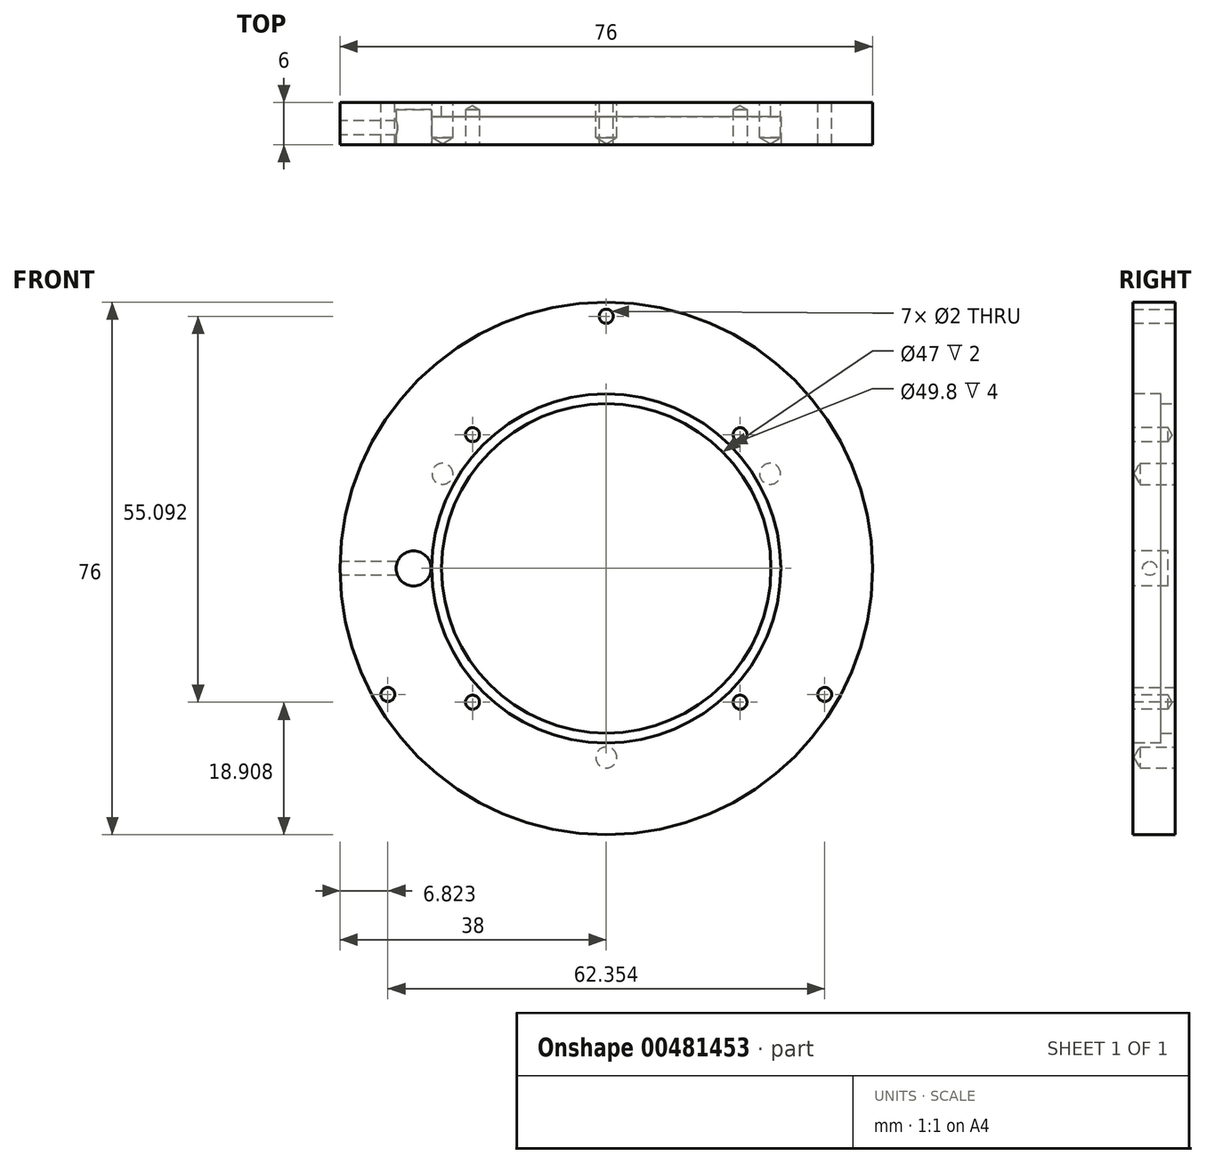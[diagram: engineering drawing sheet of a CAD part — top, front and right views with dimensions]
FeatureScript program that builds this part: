
annotation { "Feature Type Name" : "Feature", "Feature Type Description" : "" }
export const myFeature = defineFeature(function(context is Context, id is Id, definition is map)
    precondition{}
    {
        {
            var Q0;
            Q0=qCreatedBy(makeId("Front.planeOp"),FACE);
            var sketch = newSketch(context, id + "F0", { "sketchPlane" : qUnion([Q0])});
            skCircle(sketch, "E0", {"center": v(0, 0) * mm, "radius": 38 * mm});
            skCircle(sketch, "E1", {"center": v(0, 0) * mm, "radius": 23.5 * mm});
            skSolve(sketch);
        }
        {
            var Q0;
            Q0 = qSketchRegion(id + "F0", true);
            extrude(context, id + "F1", {"entities" : qUnion([Q0]), "depth" : 6 * mm});
        }
        {
            var Q0;
            Q0=makeQuery(id+"F1.opExtrude","CAP_FACE",FACE,{"disambiguationData":[OSD([sQuery(id+"F0.wireOp",EDGE,"E0"),sQuery(id+"F0.wireOp",EDGE,"E1")])],"isStart":false});
            var sketch = newSketch(context, id + "F2", { "sketchPlane" : qUnion([Q0])});
            skCircle(sketch, "E2", {"center": v(0, 0) * mm, "radius": 24.9 * mm});
            skSolve(sketch);
        }
        {
            var Q0;
            Q0 = qSketchRegion(id + "F2", true);
            extrude(context, id + "F3", {"entities" : qUnion([Q0]), "operationType" : NewBodyOperationType.REMOVE, "oppositeDirection" : true, "depth" : 4 * mm});
        }
        {
            var Q0;
            Q0=makeQuery(id+"F1.opExtrude","CAP_FACE",FACE,{"disambiguationData":[OSD([sQuery(id+"F0.wireOp",EDGE,"E0"),sQuery(id+"F0.wireOp",EDGE,"E1")])],"isStart":true});
            var sketch = newSketch(context, id + "F4", { "sketchPlane" : qUnion([Q0])});
            skPoint(sketch, "E3", {"position": v(23.38, 13.5) * mm});
            skLineSegment(sketch, "E4", {"start": v(0, 0) * mm, "end": v(35.09, 20.26) * mm, "construction": true});
            skLineSegment(sketch, "E5", {"start": v(0, 0) * mm, "end": v(-35.23, 20.34) * mm, "construction": true});
            skLineSegment(sketch, "E6", {"start": v(0, 0) * mm, "end": v(0, -41.92) * mm, "construction": true});
            skLineSegment(sketch, "E7", {"start": v(0, 0) * mm, "end": v(-35.01, -20.21) * mm, "construction": true});
            skLineSegment(sketch, "E8", {"start": v(0, 0) * mm, "end": v(34, -19.63) * mm, "construction": true});
            skLineSegment(sketch, "E9", {"start": v(0, 0) * mm, "end": v(0, 41.54) * mm, "construction": true});
            skCircle(sketch, "E10", {"center": v(0, 0) * mm, "radius": 27 * mm, "construction": true});
            skPoint(sketch, "E11", {"position": v(-23.38, 13.5) * mm});
            skPoint(sketch, "E12", {"position": v(-31.18, -18) * mm});
            skPoint(sketch, "E13", {"position": v(0, -27) * mm});
            skPoint(sketch, "E14", {"position": v(31.18, -18) * mm});
            skCircle(sketch, "E15", {"center": v(0, 0) * mm, "radius": 36 * mm, "construction": true});
            skPoint(sketch, "E16", {"position": v(0, 36) * mm});
            skSolve(sketch);
        }
        {
            var Q0;
            Q0=sQuery(id+"F4.wireOp",VERTEX,"E3");
            var Q1;
            Q1=sQuery(id+"F4.wireOp",VERTEX,"E11");
            var Q2;
            Q2=sQuery(id+"F4.wireOp",VERTEX,"E13");
            var Q3;
            Q3=makeQuery(id+"F1.opExtrude","SWEPT_BODY",BODY,{"disambiguationData":[OSD([sQuery(id+"F0.wireOp",EDGE,"E0"),sQuery(id+"F0.wireOp",EDGE,"E1")])]});
            hole(context, id + "F5", {"style" : HoleStyle.SIMPLE, "endStyle" : HoleEndStyle.BLIND, "holeDiameter" : 3 * mm, "holeDepth" : 5 * mm, "isTappedThrough" : true, "tappedDepth" : 12 * mm, "tapClearance" : 3, "locations" : qUnion([Q0, Q1, Q2]), "scope" : qUnion([Q3])});
        }
        {
            var Q0;
            Q0=sQuery(id+"F4.wireOp",VERTEX,"E16");
            var Q1;
            Q1=sQuery(id+"F4.wireOp",VERTEX,"E12");
            var Q2;
            Q2=sQuery(id+"F4.wireOp",VERTEX,"E14");
            var Q3;
            Q3=makeQuery(id+"F1.opExtrude","SWEPT_BODY",BODY,{"disambiguationData":[OSD([sQuery(id+"F0.wireOp",EDGE,"E0"),sQuery(id+"F0.wireOp",EDGE,"E1")])]});
            hole(context, id + "F6", {"style" : HoleStyle.SIMPLE, "endStyle" : HoleEndStyle.THROUGH, "holeDiameter" : 2 * mm, "isTappedThrough" : true, "tappedDepth" : 12 * mm, "tapClearance" : 3, "locations" : qUnion([Q0, Q1, Q2]), "scope" : qUnion([Q3])});
        }
        {
            var Q0;
            Q0=makeQuery(id+"F1.opExtrude","CAP_FACE",FACE,{"disambiguationData":[OSD([sQuery(id+"F0.wireOp",EDGE,"E0"),sQuery(id+"F0.wireOp",EDGE,"E1")])],"isStart":false});
            var sketch = newSketch(context, id + "F7", { "sketchPlane" : qUnion([Q0])});
            skCircle(sketch, "E17", {"center": v(0, 0) * mm, "radius": 27 * mm, "construction": true});
            skLineSegment(sketch, "E18", {"start": v(0, 0) * mm, "end": v(37.63, 37.63) * mm, "construction": true});
            skLineSegment(sketch, "E19", {"start": v(-32.63, -32.63) * mm, "end": v(0, 0) * mm, "construction": true});
            skLineSegment(sketch, "E20", {"start": v(35.9, -35.9) * mm, "end": v(0, 0) * mm, "construction": true});
            skLineSegment(sketch, "E21", {"start": v(-42.59, 42.59) * mm, "end": v(0, 0) * mm, "construction": true});
            skPoint(sketch, "E22", {"position": v(-19.1, 19.1) * mm});
            skPoint(sketch, "E23", {"position": v(19.1, 19.1) * mm});
            skPoint(sketch, "E24", {"position": v(19.1, -19.1) * mm});
            skPoint(sketch, "E25", {"position": v(-19.1, -19.1) * mm});
            skSolve(sketch);
        }
        {
            var Q0;
            Q0=sQuery(id+"F7.wireOp",VERTEX,"E22");
            var Q1;
            Q1=sQuery(id+"F7.wireOp",VERTEX,"E25");
            var Q2;
            Q2=sQuery(id+"F7.wireOp",VERTEX,"E24");
            var Q3;
            Q3=sQuery(id+"F7.wireOp",VERTEX,"E23");
            var Q4;
            Q4=makeQuery(id+"F1.opExtrude","SWEPT_BODY",BODY,{"disambiguationData":[OSD([sQuery(id+"F0.wireOp",EDGE,"E0"),sQuery(id+"F0.wireOp",EDGE,"E1")])]});
            hole(context, id + "F8", {"style" : HoleStyle.SIMPLE, "endStyle" : HoleEndStyle.BLIND, "holeDiameter" : 2 * mm, "holeDepth" : 5 * mm, "isTappedThrough" : true, "tappedDepth" : 12 * mm, "tapClearance" : 3, "locations" : qUnion([Q0, Q1, Q2, Q3]), "scope" : qUnion([Q4])});
        }
        {
            var Q0;
            Q0=makeQuery(id+"F1.opExtrude","CAP_FACE",FACE,{"disambiguationData":[OSD([sQuery(id+"F0.wireOp",EDGE,"E0"),sQuery(id+"F0.wireOp",EDGE,"E1")])],"isStart":false});
            var sketch = newSketch(context, id + "F9", { "sketchPlane" : qUnion([Q0])});
            skCircle(sketch, "E26", {"center": v(-27.5, 0) * mm, "radius": 2.5 * mm});
            skSolve(sketch);
        }
        {
            var Q0;
            Q0 = qSketchRegion(id + "F9", true);
            extrude(context, id + "F10", {"entities" : qUnion([Q0]), "operationType" : NewBodyOperationType.REMOVE, "oppositeDirection" : true, "depth" : 5 * mm});
        }
        {
            var Q0;
            Q0=qCreatedBy(makeId("Right.planeOp"),FACE);
            cPlane(context, id + "F11", {"entities" : qUnion([Q0]), "cplaneType" : CPlaneType.OFFSET, "offset" : 40 * mm, "oppositeDirection" : true, "width" : 150 * mm, "height" : 150 * mm});
        }
        {
            var Q0;
            Q0=qCreatedBy(id+"F11.planeOp",FACE);
            var sketch = newSketch(context, id + "F12", { "sketchPlane" : qUnion([Q0])});
            skPoint(sketch, "E27", {"position": v(-3.6, 0) * mm});
            skSolve(sketch);
        }
        {
            var Q0;
            Q0=sQuery(id+"F12.wireOp",VERTEX,"E27");
            var Q1;
            Q1=makeQuery(id+"F1.opExtrude","SWEPT_BODY",BODY,{"disambiguationData":[OSD([sQuery(id+"F0.wireOp",EDGE,"E0"),sQuery(id+"F0.wireOp",EDGE,"E1")])]});
            hole(context, id + "F13", {"style" : HoleStyle.SIMPLE, "endStyle" : HoleEndStyle.BLIND, "oppositeDirection" : true, "holeDiameter" : 2 * mm, "holeDepth" : 10 * mm, "isTappedThrough" : true, "tappedDepth" : 12 * mm, "tapClearance" : 3, "locations" : qUnion([Q0]), "scope" : qUnion([Q1])});
        }
    });
